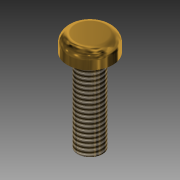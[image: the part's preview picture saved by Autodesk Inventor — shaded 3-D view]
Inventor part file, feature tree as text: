
AUTODESK INVENTOR PART (.ipt)
format: ipt  version: 2015 (Build 190159000, 159)  size: 121,856 bytes
history: native  units: mm
features: extrude x2, sketch x2, other x1, fillet x1, thread x1
ambient origin geometry x8: Origin, YZ Plane, XZ Plane, XY Plane, X Axis, Y Axis, Z Axis, Center Point
bodies: Body1 (feature_tree)
feature tree (7):
  other  "ソリッド1"
  extrude  "押し出し1"  Depth=5.5mm
  fillet  "フィレット1"  Radius=2.0mm
  extrude  "押し出し2"  Depth=1.0mm
  thread  "ねじ1"
  sketch  "スケッチ1"
  sketch  "スケッチ2"
